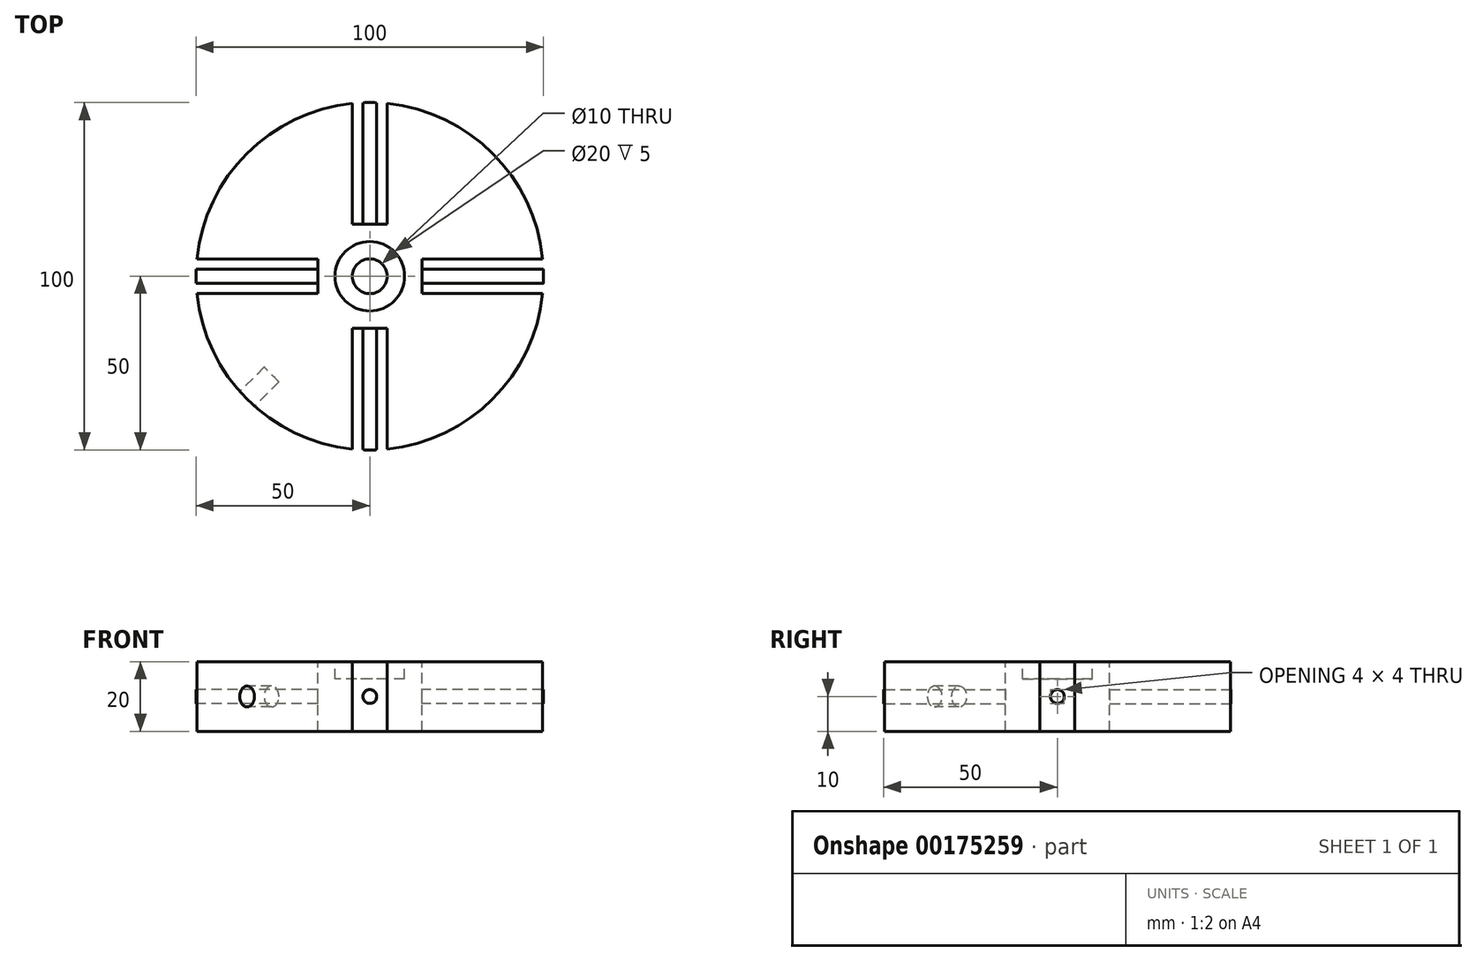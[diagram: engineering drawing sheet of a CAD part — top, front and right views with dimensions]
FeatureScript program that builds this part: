
annotation { "Feature Type Name" : "Feature", "Feature Type Description" : "" }
export const myFeature = defineFeature(function(context is Context, id is Id, definition is map)
    precondition{}
    {
        {
            var Q0;
            Q0=qCreatedBy(makeId("Top.planeOp"),FACE);
            var sketch = newSketch(context, id + "F0", { "sketchPlane" : qUnion([Q0])});
            skCircle(sketch, "E0", {"center": v(0, 0) * mm, "radius": 50 * mm});
            skSolve(sketch);
        }
        {
            var Q0;
            Q0 = qSketchRegion(id + "F0", true);
            extrude(context, id + "F1", {"entities" : qUnion([Q0]), "depth" : 20 * mm});
        }
        {
            var Q0;
            Q0=makeQuery(id+"F1.opExtrude","CAP_FACE",FACE,{"disambiguationData":[OSD([sQuery(id+"F0.wireOp",EDGE,"E0")])],"isStart":false});
            var sketch = newSketch(context, id + "F2", { "sketchPlane" : qUnion([Q0])});
            skLineSegment(sketch, "E1", {"start": v(0, 50) * mm, "end": v(0, 15) * mm, "construction": true});
            skLineSegment(sketch, "E2", {"start": v(-50, 0) * mm, "end": v(50, 0) * mm, "construction": true});
            skLineSegment(sketch, "E3.0", {"start": v(-5, 49.75) * mm, "end": v(-5, 15) * mm});
            skLineSegment(sketch, "E4.0", {"start": v(5, 49.75) * mm, "end": v(5, 15) * mm});
            skArc(sketch, "E5", {"start": v(5, 49.75) * mm, "mid": v(0, 50) * mm, "end": v(-5, 49.75) * mm});
            skArc(sketch, "E6", {"start": v(-5, -49.75) * mm, "mid": v(0, -50) * mm, "end": v(5, -49.75) * mm});
            skLineSegment(sketch, "E7.1.0", {"start": v(50, 0) * mm, "end": v(15, 0) * mm, "construction": true});
            skLineSegment(sketch, "E7.1.1", {"start": v(49.75, 5) * mm, "end": v(15, 5) * mm});
            skLineSegment(sketch, "E7.1.2", {"start": v(49.75, -5) * mm, "end": v(15, -5) * mm});
            skLineSegment(sketch, "E7.anchor1", {"start": v(0, 0) * mm, "end": v(0, -50) * mm, "construction": true});
            skLineSegment(sketch, "E7.anchor2", {"start": v(0, 0) * mm, "end": v(-50, 0) * mm, "construction": true});
            skArc(sketch, "E8", {"start": v(49.75, -5) * mm, "mid": v(50, 0) * mm, "end": v(49.75, 5) * mm});
            skArc(sketch, "E9", {"start": v(-49.75, 5) * mm, "mid": v(-50, 0) * mm, "end": v(-49.75, -5) * mm});
            skLineSegment(sketch, "E10.bottom", {"start": v(15, -15) * mm, "end": v(5, -15) * mm, "construction": true});
            skLineSegment(sketch, "E10.top", {"start": v(15, 15) * mm, "end": v(5, 15) * mm, "construction": true});
            skLineSegment(sketch, "E10.left", {"start": v(15, -15) * mm, "end": v(15, -5) * mm, "construction": true});
            skLineSegment(sketch, "E10.right", {"start": v(-15, -15) * mm, "end": v(-15, -5) * mm, "construction": true});
            skLineSegment(sketch, "E11.trimOffspring", {"start": v(-5, 5) * mm, "end": v(-5, -5) * mm, "construction": true});
            skLineSegment(sketch, "E12.trimOffspring", {"start": v(0, 5) * mm, "end": v(0, -5) * mm, "construction": true});
            skLineSegment(sketch, "E13.trimOffspring", {"start": v(5, 5) * mm, "end": v(5, -5) * mm, "construction": true});
            skLineSegment(sketch, "E14.trimOffspring", {"start": v(5, 5) * mm, "end": v(-5, 5) * mm, "construction": true});
            skLineSegment(sketch, "E15.trimOffspring", {"start": v(5, 0) * mm, "end": v(-50, 0) * mm, "construction": true});
            skLineSegment(sketch, "E16.trimOffspring", {"start": v(5, -5) * mm, "end": v(-5, -5) * mm, "construction": true});
            skLineSegment(sketch, "E17.trimOffspring", {"start": v(5, -15) * mm, "end": v(5, -49.75) * mm});
            skLineSegment(sketch, "E18.trimOffspring", {"start": v(0, -15) * mm, "end": v(0, -50) * mm, "construction": true});
            skLineSegment(sketch, "E19.trimOffspring", {"start": v(-5, -15) * mm, "end": v(-5, -49.75) * mm});
            skLineSegment(sketch, "E20.trimOffspring", {"start": v(-15, -5) * mm, "end": v(-15, -5) * mm});
            skLineSegment(sketch, "E21.trimOffspring", {"start": v(-15, 5) * mm, "end": v(-49.75, 5) * mm});
            skLineSegment(sketch, "E22", {"start": v(-5, 15) * mm, "end": v(-15, 15) * mm, "construction": true});
            skLineSegment(sketch, "E23", {"start": v(5, 15) * mm, "end": v(-5, 15) * mm});
            skLineSegment(sketch, "E24", {"start": v(15, 5) * mm, "end": v(15, 15) * mm, "construction": true});
            skLineSegment(sketch, "E25", {"start": v(15, -5) * mm, "end": v(15, 5) * mm});
            skLineSegment(sketch, "E26", {"start": v(5, -15) * mm, "end": v(-5, -15) * mm});
            skLineSegment(sketch, "E27", {"start": v(-5, -15) * mm, "end": v(-15, -15) * mm, "construction": true});
            skLineSegment(sketch, "E28", {"start": v(-15, -5) * mm, "end": v(-49.75, -5) * mm});
            skLineSegment(sketch, "E29", {"start": v(-15, 5) * mm, "end": v(-15, 15) * mm, "construction": true});
            skLineSegment(sketch, "E30", {"start": v(-15, -5) * mm, "end": v(-15, 5) * mm});
            skSolve(sketch);
        }
        {
            var Q0;
            Q0 = qSketchRegion(id + "F2", true);
            extrude(context, id + "F3", {"entities" : qUnion([Q0]), "operationType" : NewBodyOperationType.REMOVE, "endBound" : BoundingType.THROUGH_ALL, "oppositeDirection" : true, "depth" : 25 * mm});
        }
        {
            var Q0;
            Q0=makeQuery(id+"F3.boolean.opBoolean","COPY",FACE,{"derivedFrom":makeQuery(id+"F3.opExtrude","SWEPT_FACE",FACE,{"disambiguationData":[OSD([sQuery(id+"F2.wireOp",EDGE,"E23")])]})});
            var sketch = newSketch(context, id + "F4", { "sketchPlane" : qUnion([Q0])});
            skLineSegment(sketch, "E31", {"start": v(0, 20) * mm, "end": v(0, 0) * mm, "construction": true});
            skLineSegment(sketch, "E32", {"start": v(0, 10) * mm, "end": v(-5, 10) * mm, "construction": true});
            skCircle(sketch, "E33", {"center": v(0, 10) * mm, "radius": 2 * mm});
            skSolve(sketch);
        }
        {
            var Q0;
            Q0 = qSketchRegion(id + "F4", true);
            var Q1;
            {var subQ0=sQuery(id+"F0.wireOp",EDGE,"E0");Q1=makeQuery(id+"F3.boolean.opBoolean","SPLIT",FACE,{"disambiguationData":[TD([makeQuery(id+"F3.opExtrude","SWEPT_FACE",FACE,{"disambiguationData":[OSD([sQuery(id+"F2.wireOp",EDGE,"E19.trimOffspring")])]})])],"derivedFrom":makeQuery(id+"F1.opExtrude","SWEPT_FACE",FACE,{"disambiguationData":[OSD([subQ0])]})});}
            var Q2;
            {var subQ0=sQuery(id+"F0.wireOp",EDGE,"E0");Q2=makeQuery(id+"F3.boolean.opBoolean","SPLIT",FACE,{"disambiguationData":[TD([makeQuery(id+"F3.opExtrude","SWEPT_FACE",FACE,{"disambiguationData":[OSD([sQuery(id+"F2.wireOp",EDGE,"E3.0")])]})])],"derivedFrom":makeQuery(id+"F1.opExtrude","SWEPT_FACE",FACE,{"disambiguationData":[OSD([subQ0])]})});}
            extrude(context, id + "F5", {"entities" : qUnion([Q0]), "operationType" : NewBodyOperationType.ADD, "endBound" : BoundingType.UP_TO_SURFACE, "oppositeDirection" : true, "endBoundEntityFace" : qUnion([Q1]), "depth" : 25 * mm, "hasSecondDirection" : true, "secondDirectionBound" : SecondDirectionBoundingType.UP_TO_SURFACE, "secondDirectionOppositeDirection" : false, "secondDirectionBoundEntityFace" : qUnion([Q2]), "secondDirectionDepth" : 25 * mm});
        }
        {
            var Q0;
            Q0=makeQuery(id+"F3.boolean.opBoolean","COPY",FACE,{"derivedFrom":makeQuery(id+"F3.opExtrude","SWEPT_FACE",FACE,{"disambiguationData":[OSD([sQuery(id+"F2.wireOp",EDGE,"E30")])]})});
            var sketch = newSketch(context, id + "F6", { "sketchPlane" : qUnion([Q0])});
            skCircle(sketch, "E34", {"center": v(0, 10) * mm, "radius": 2 * mm});
            skLineSegment(sketch, "E35", {"start": v(0, 10) * mm, "end": v(5, 10) * mm, "construction": true});
            skLineSegment(sketch, "E36", {"start": v(0, 0) * mm, "end": v(0, 10) * mm, "construction": true});
            skSolve(sketch);
        }
        {
            var Q0;
            Q0 = qSketchRegion(id + "F6", true);
            var Q1;
            {var subQ0=sQuery(id+"F0.wireOp",EDGE,"E0");Q1=makeQuery(id+"F3.boolean.opBoolean","SPLIT",FACE,{"disambiguationData":[TD([makeQuery(id+"F3.opExtrude","SWEPT_FACE",FACE,{"disambiguationData":[OSD([sQuery(id+"F2.wireOp",EDGE,"E4.0")])]})])],"derivedFrom":makeQuery(id+"F1.opExtrude","SWEPT_FACE",FACE,{"disambiguationData":[OSD([subQ0])]})});}
            var Q2;
            {var subQ0=sQuery(id+"F0.wireOp",EDGE,"E0");Q2=makeQuery(id+"F3.boolean.opBoolean","SPLIT",FACE,{"disambiguationData":[TD([makeQuery(id+"F3.opExtrude","SWEPT_FACE",FACE,{"disambiguationData":[OSD([sQuery(id+"F2.wireOp",EDGE,"E3.0")])]})])],"derivedFrom":makeQuery(id+"F1.opExtrude","SWEPT_FACE",FACE,{"disambiguationData":[OSD([subQ0])]})});}
            extrude(context, id + "F7", {"entities" : qUnion([Q0]), "operationType" : NewBodyOperationType.ADD, "endBound" : BoundingType.UP_TO_SURFACE, "oppositeDirection" : true, "endBoundEntityFace" : qUnion([Q1]), "depth" : 25 * mm, "hasSecondDirection" : true, "secondDirectionBound" : SecondDirectionBoundingType.UP_TO_SURFACE, "secondDirectionOppositeDirection" : false, "secondDirectionBoundEntityFace" : qUnion([Q2]), "secondDirectionDepth" : 25 * mm});
        }
        {
            var Q0;
            Q0=makeQuery(id+"F1.opExtrude","CAP_FACE",FACE,{"disambiguationData":[OSD([sQuery(id+"F0.wireOp",EDGE,"E0")])],"isStart":true});
            var sketch = newSketch(context, id + "F8", { "sketchPlane" : qUnion([Q0])});
            skCircle(sketch, "E37", {"center": v(0, 0) * mm, "radius": 5 * mm});
            skSolve(sketch);
        }
        {
            var Q0;
            Q0 = qSketchRegion(id + "F8", true);
            extrude(context, id + "F9", {"entities" : qUnion([Q0]), "operationType" : NewBodyOperationType.REMOVE, "endBound" : BoundingType.THROUGH_ALL, "oppositeDirection" : true, "depth" : 25 * mm});
        }
        {
            var Q0;
            Q0=makeQuery(id+"F1.opExtrude","CAP_FACE",FACE,{"disambiguationData":[OSD([sQuery(id+"F0.wireOp",EDGE,"E0")])],"isStart":false});
            var sketch = newSketch(context, id + "F10", { "sketchPlane" : qUnion([Q0])});
            skCircle(sketch, "E38", {"center": v(0, 0) * mm, "radius": 10 * mm});
            skSolve(sketch);
        }
        {
            var Q0;
            Q0 = qSketchRegion(id + "F10", true);
            extrude(context, id + "F11", {"entities" : qUnion([Q0]), "operationType" : NewBodyOperationType.REMOVE, "oppositeDirection" : true, "depth" : 5 * mm});
        }
        {
            var Q0;
            Q0=qCreatedBy(makeId("Right.planeOp"),FACE);
            var sketch = newSketch(context, id + "F12", { "sketchPlane" : qUnion([Q0])});
            skLineSegment(sketch, "E39", {"start": v(0, 0) * mm, "end": v(0, 20) * mm, "construction": true});
            skSolve(sketch);
        }
        {
            var Q0;
            Q0=qCreatedBy(makeId("Right.planeOp"),FACE);
            var Q1;
            Q1=sQuery(id+"F12.wireOp",EDGE,"E39");
            cPlane(context, id + "F13", {"entities" : qUnion([Q0, Q1]), "cplaneType" : CPlaneType.LINE_ANGLE, "offset" : 25 * mm, "angle" : 45 * degree, "width" : 150 * mm, "height" : 150 * mm});
        }
        {
            var Q0;
            Q0=qCreatedBy(id+"F13.planeOp",FACE);
            cPlane(context, id + "F14", {"entities" : qUnion([Q0]), "cplaneType" : CPlaneType.OFFSET, "offset" : 50 * mm, "width" : 150 * mm, "height" : 150 * mm});
        }
        {
            var Q0;
            Q0=qCreatedBy(id+"F14.planeOp",FACE);
            var sketch = newSketch(context, id + "F15", { "sketchPlane" : qUnion([Q0])});
            skCircle(sketch, "E40", {"center": v(0, 10) * mm, "radius": 3 * mm});
            skLineSegment(sketch, "E41", {"start": v(0, 0) * mm, "end": v(0, 10) * mm, "construction": true});
            skLineSegment(sketch, "E42", {"start": v(0, 10) * mm, "end": v(0, 20) * mm, "construction": true});
            skSolve(sketch);
        }
        {
            var Q0;
            Q0 = qSketchRegion(id + "F15", true);
            extrude(context, id + "F16", {"entities" : qUnion([Q0]), "operationType" : NewBodyOperationType.REMOVE, "oppositeDirection" : true, "depth" : 10 * mm});
        }
    });
